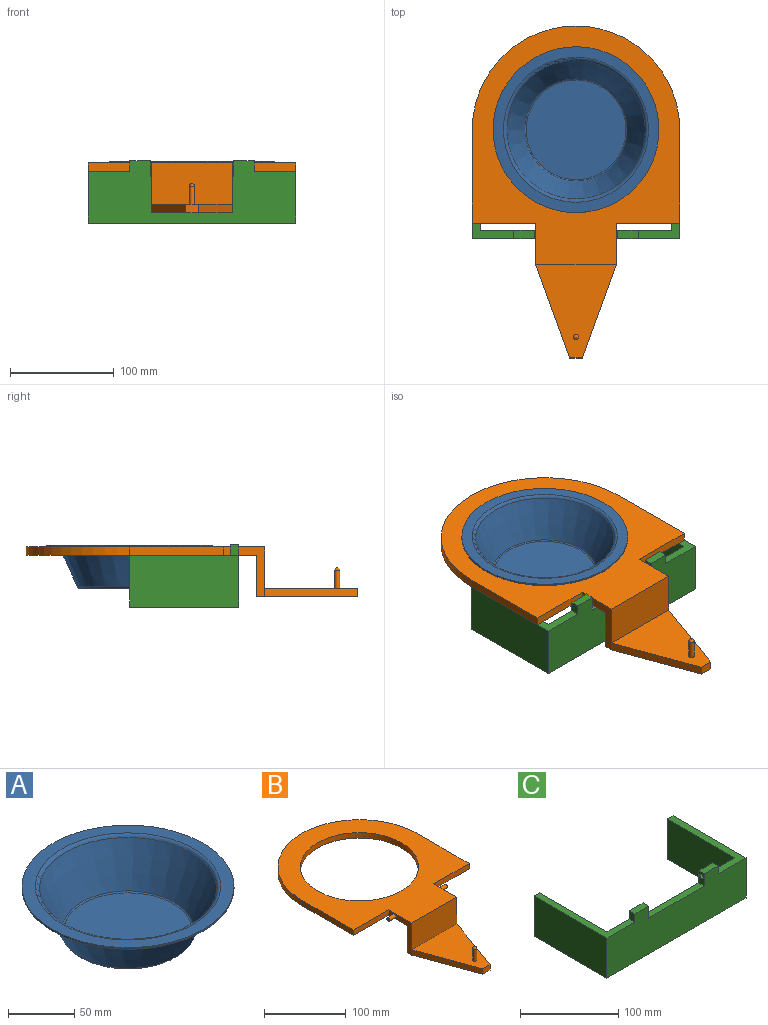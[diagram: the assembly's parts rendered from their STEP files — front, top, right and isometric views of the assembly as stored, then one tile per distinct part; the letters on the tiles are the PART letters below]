
ASSEMBLY  parts=3 mates=3
PART A: 11 faces, bbox 160x160x41.5 mm
  f0: cylinder r=80mm len=160mm, axis (0,0,1), area 754mm2, adj f5,f10
  f1: cone r=66.75mm half-angle=25deg, axis (0,0,1), area 14949.2mm2, adj f2,f4
  f2: torus R=48.09mm, axis (0,0,-1), area 522.3mm2, adj f1,f3
  f3: plane 96.18x96.18mm, normal (0,0,1), area 7265mm2, adj f2
  f4: torus R=69.93mm, axis (0,0,-1), area 1700.1mm2, adj f1,f5
  f5: plane 160x160mm, normal (0,0,1), area 4744.7mm2, adj f0,f4
  f6: cone r=68.11mm half-angle=25deg, axis (0,0,1), area 15299mm2, adj f7,f9
  f7: torus R=48.09mm, axis (0,0,-1), area 1061mm2, adj f6,f8
  f8: plane 96.18x96.18mm, normal (0,0,-1), area 7265mm2, adj f7
  f9: torus R=69.93mm, axis (0,0,-1), area 982.4mm2, adj f6,f10
  f10: plane 160x160mm, normal (0,0,-1), area 4744.7mm2, adj f0,f9
PART B: 23 faces, bbox 200x320x48 mm
  f0: plane 12.49x8mm, normal (0,-1,0), area 99.9mm2, adj f2,f3,f21,f22
  f1: plane 48x40mm, normal (1,0,0), area 620.4mm2, adj f2,f4,f7,f8,f13,f16,f20,f21
  f2: plane 98x78mm, normal (0,0,-1), area 4695.8mm2, adj f0,f1,f10,f20,f21,f22
  f3: plane 90x78mm, normal (0,0,1), area 4052.2mm2, adj f0,f8,f18,f21,f22
  f4: plane 222x200mm, normal (0,0,-1), area 19691mm2, adj f1,f5,f6,f9,f10,f11,f12,f13
  f5: plane 90x8mm, normal (1,0,0), area 720mm2, adj f4,f7,f9,f13
  f6: plane 90x8mm, normal (-1,0,0), area 720mm2, adj f4,f7,f9,f12
  f7: plane 230x200mm, normal (0,0,1), area 20315mm2, adj f1,f5,f6,f8,f9,f10,f11,f12
  f8: plane 78x40mm, normal (0,-1,0), area 3120mm2, adj f1,f3,f7,f10
  f9: cylinder r=100mm len=200mm, axis (0,0,-1), area 2513.3mm2, adj f4,f5,f6,f7
  f10: plane 48x40mm, normal (-1,0,0), area 620.4mm2, adj f2,f4,f7,f8,f12,f15,f20,f22
  f11: cylinder r=72.5mm len=145mm, axis (0,0,-1), area 3644.2mm2, adj f4,f7
  f12: plane 61x8mm, normal (0,-1,0), area 488mm2, adj f4,f6,f7,f10
  f13: plane 61x8mm, normal (0,-1,0), area 488mm2, adj f1,f4,f5,f7
  f14: plane 5x5mm, normal (-1,0,0), area 19.6mm2, adj f15
  f15: cylinder r=2.5mm len=11mm, axis (-1,0,0), area 172.8mm2, adj f10,f14
  f16: cylinder r=2.5mm len=11mm, axis (-1,0,0), area 172.8mm2, adj f1,f17
  f17: plane 5x5mm, normal (1,0,0), area 19.6mm2, adj f16
  f18: cylinder r=2.5mm len=17.5mm, axis (0,0,-1), area 274.9mm2, adj f3,f19
  f19: sphere r=2.5mm, area 39.3mm2, adj f18
  f20: plane 78x40mm, normal (0,1,0), area 3120mm2, adj f1,f2,f4,f10
  f21: plane 90x32.76mm, normal (0.94,-0.34,0), area 766.2mm2, adj f0,f1,f2,f3
  f22: plane 90x32.76mm, normal (-0.94,-0.34,0), area 766.2mm2, adj f0,f2,f3,f10
PART C: 22 faces, bbox 200x105x60 mm
  f0: plane 105x40mm, normal (0,0,1), area 1096mm2, adj f4,f5,f6,f8,f9,f11
  f1: plane 200x105mm, normal (0,0,-1), area 3152mm2, adj f2,f4,f5,f6,f7,f8,f9,f10
  f2: plane 50x8mm, normal (0,1,0), area 400mm2, adj f1,f3,f7,f10
  f3: plane 105x40mm, normal (0,0,1), area 1096mm2, adj f2,f6,f7,f9,f10,f15
  f4: plane 50x8mm, normal (0,1,0), area 400mm2, adj f0,f1,f5,f8
  f5: plane 105x50mm, normal (-1,0,0), area 5250mm2, adj f0,f1,f4,f6
  f6: plane 200x60mm, normal (0,-1,0), area 10000mm2, adj f0,f1,f3,f5,f7,f11,f12,f13
  f7: plane 105x50mm, normal (1,0,0), area 5250mm2, adj f1,f2,f3,f6
  f8: plane 97x50mm, normal (1,0,0), area 4850mm2, adj f0,f1,f4,f9
  f9: plane 184x60mm, normal (0,1,0), area 9200mm2, adj f0,f1,f3,f8,f10,f11,f12,f13
  f10: plane 97x50mm, normal (-1,0,0), area 4850mm2, adj f1,f2,f3,f9
  f11: plane 10x8mm, normal (-1,0,0), area 80mm2, adj f0,f6,f9,f13
  f12: plane 15x8mm, normal (1,0,0), area 100.4mm2, adj f6,f9,f13,f17,f20
  f13: plane 20x8mm, normal (0,0,1), area 160mm2, adj f6,f9,f11,f12
  f14: plane 15x8mm, normal (-1,0,0), area 100.4mm2, adj f6,f9,f16,f17,f19
  f15: plane 10x8mm, normal (1,0,0), area 80mm2, adj f3,f6,f9,f16
  f16: plane 20x8mm, normal (0,0,1), area 160mm2, adj f6,f9,f14,f15
  f17: plane 80x8mm, normal (0,0,1), area 640mm2, adj f6,f9,f12,f14
  f18: plane 5x5mm, normal (-1,0,0), area 19.6mm2, adj f19
  f19: cylinder r=2.5mm len=10mm, axis (1,0,0), area 157.1mm2, adj f14,f18
  f20: cylinder r=2.5mm len=10mm, axis (1,0,0), area 157.1mm2, adj f12,f21
  f21: plane 5x5mm, normal (1,0,0), area 19.6mm2, adj f20
PLACE A t=(0,0,58)mm
PLACE B t=(0,0,50)mm
PLACE C at identity fixed
MATE planar C.f0 <-> B.f11  axis (0,0,1) through (-91.33,-63.83,50)mm
MATE revolute B.f15 <-> C.f19  axis (-1,0,0) through (-39,-100,54)mm
MATE fastened A.f0 <-> B.f11  axis (0,0,-1) through (0,0,58)mm
